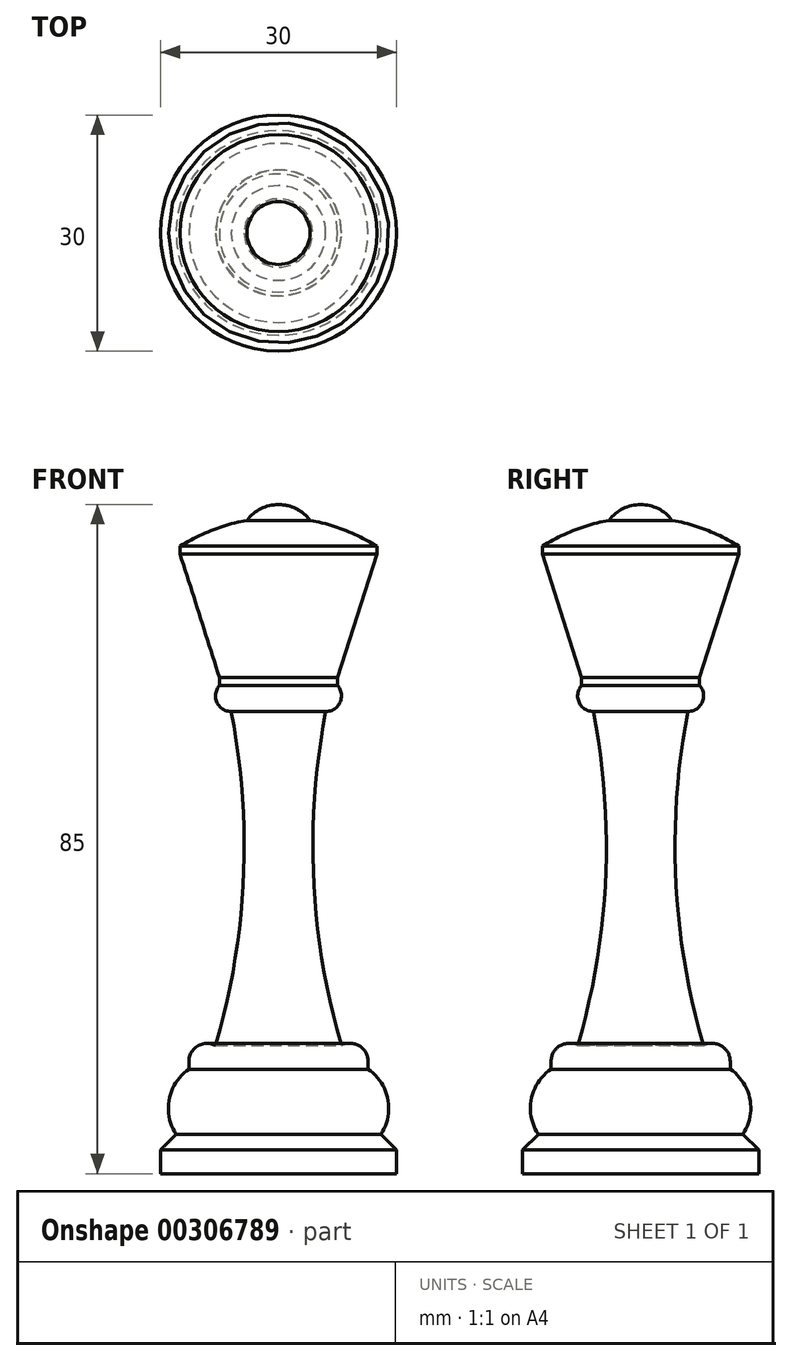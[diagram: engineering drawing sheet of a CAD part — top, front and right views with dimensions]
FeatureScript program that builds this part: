
annotation { "Feature Type Name" : "Feature", "Feature Type Description" : "" }
export const myFeature = defineFeature(function(context is Context, id is Id, definition is map)
    precondition{}
    {
        {
            var Q0;
            Q0=qCreatedBy(makeId("Front.planeOp"),FACE);
            var sketch = newSketch(context, id + "F0", { "sketchPlane" : qUnion([Q0])});
            skArc(sketch, "E0", {"start": v(12.5, -5.27) * mm, "mid": v(8.4, -3.24) * mm, "end": v(4, -2) * mm});
            skLineSegment(sketch, "E1", {"start": v(12.5, -5.27) * mm, "end": v(12.5, -6.27) * mm});
            skLineSegment(sketch, "E2", {"start": v(12.5, -6.27) * mm, "end": v(7.5, -21.97) * mm});
            skLineSegment(sketch, "E3", {"start": v(7.5, -21.97) * mm, "end": v(7.5, -22.97) * mm});
            skArc(sketch, "E4", {"start": v(6, -26.3) * mm, "mid": v(4.46, -47.63) * mm, "end": v(8, -68.72) * mm});
            skLineSegment(sketch, "E5", {"start": v(11.38, -70.72) * mm, "end": v(11.38, -71.72) * mm});
            skArc(sketch, "E6", {"start": v(13, -80) * mm, "mid": v(13.89, -75.53) * mm, "end": v(11.38, -71.72) * mm});
            skLineSegment(sketch, "E7", {"start": v(13, -80) * mm, "end": v(15, -82) * mm});
            skLineSegment(sketch, "E8", {"start": v(15, -82) * mm, "end": v(15, -85) * mm});
            skLineSegment(sketch, "E9", {"start": v(15, -85) * mm, "end": v(0, -85) * mm});
            skLineSegment(sketch, "E10", {"start": v(0, -85) * mm, "end": v(0, 0) * mm});
            skArc(sketch, "E11", {"start": v(6, -26.3) * mm, "mid": v(7.82, -25.12) * mm, "end": v(7.5, -22.97) * mm});
            skArc(sketch, "E12", {"start": v(11.38, -70.72) * mm, "mid": v(10.26, -68.76) * mm, "end": v(8, -68.72) * mm});
            skArc(sketch, "E13", {"start": v(4, -2) * mm, "mid": v(2.24, -0.53) * mm, "end": v(0, 0) * mm});
            skSolve(sketch);
        }
        {
            var Q0;
            Q0=makeQuery(id+"F0.imprint","IMPRINT",FACE,{"disambiguationData":[TD([[makeQuery(id+"F0.imprint","IMPRINT",EDGE,{"derivedFrom":sQuery(id+"F0.wireOp",EDGE,"E0")}),1.0]])]});
            var Q1;
            Q1=sQuery(id+"F0.wireOp",EDGE,"E10");
            revolve(context, id + "F1", {"entities" : qUnion([Q0]), "axis" : qUnion([Q1]), "revolveType" : RevolveType.FULL});
        }
    });
